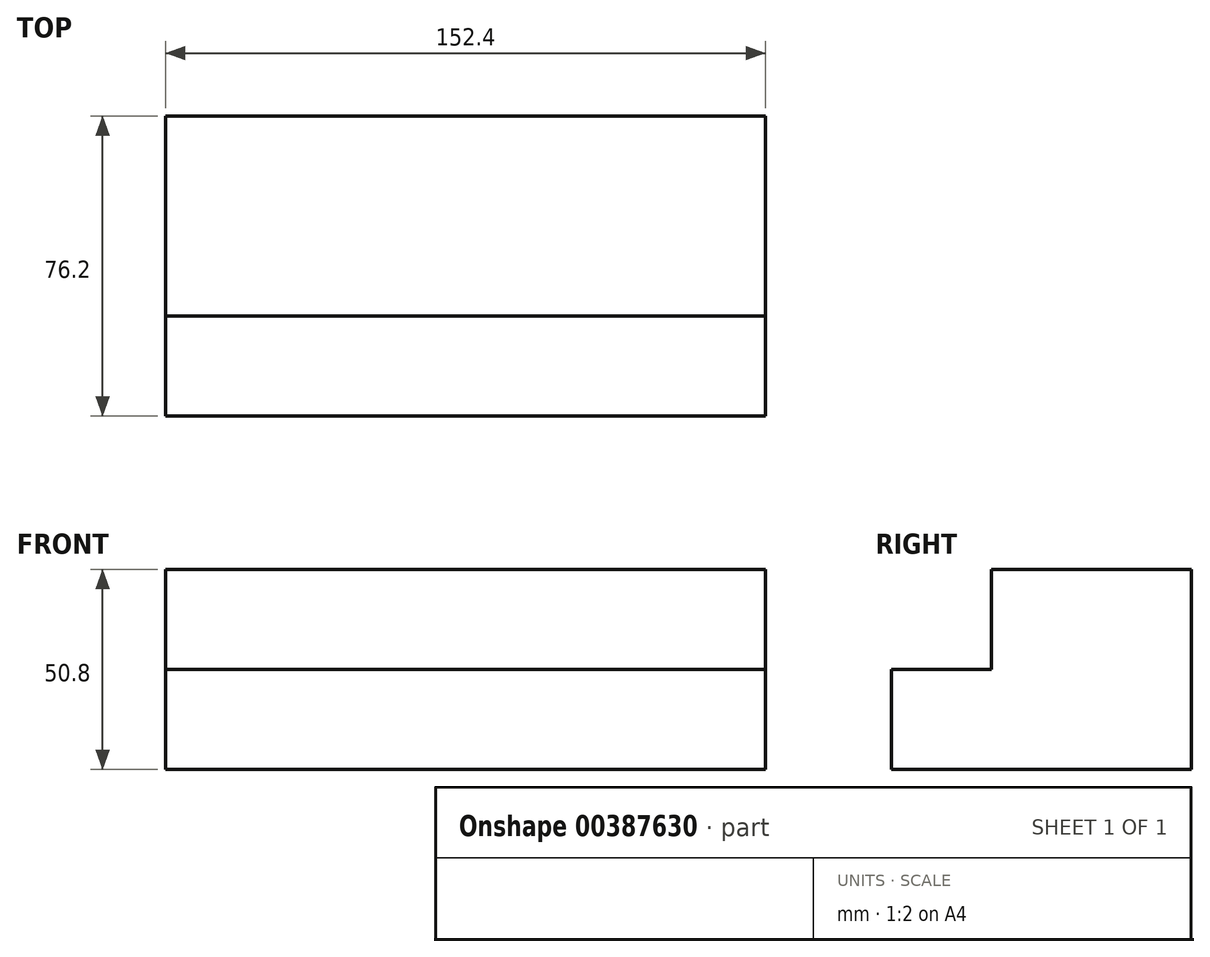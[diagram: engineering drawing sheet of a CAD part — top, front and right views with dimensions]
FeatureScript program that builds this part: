
annotation { "Feature Type Name" : "Feature", "Feature Type Description" : "" }
export const myFeature = defineFeature(function(context is Context, id is Id, definition is map)
    precondition{}
    {
        {
            var Q0;
            Q0=qCreatedBy(makeId("Top.planeOp"),FACE);
            var sketch = newSketch(context, id + "F0", { "sketchPlane" : qUnion([Q0])});
            skLineSegment(sketch, "E0.bottom", {"start": v(-152.4, -81.96) * mm, "end": v(0, -81.96) * mm});
            skLineSegment(sketch, "E0.top", {"start": v(-152.4, -5.76) * mm, "end": v(0, -5.76) * mm});
            skLineSegment(sketch, "E0.left", {"start": v(-152.4, -81.96) * mm, "end": v(-152.4, -5.76) * mm});
            skLineSegment(sketch, "E0.right", {"start": v(0, -81.96) * mm, "end": v(0, -5.76) * mm});
            skSolve(sketch);
        }
        {
            var Q0;
            Q0=qSketchRegion(id+"F0",true);
            extrude(context, id + "F1", {"entities" : qUnion([Q0]), "depth" : 25.4 * mm});
        }
        {
            var Q0;
            Q0=makeQuery(id+"F1.opExtrude","CAP_FACE",FACE,{"disambiguationData":[OSD([sQuery(id+"F0.wireOp",EDGE,"E0.bottom"),sQuery(id+"F0.wireOp",EDGE,"E0.top"),sQuery(id+"F0.wireOp",EDGE,"E0.left"),sQuery(id+"F0.wireOp",EDGE,"E0.right")])],"isStart":false});
            var sketch = newSketch(context, id + "F2", { "sketchPlane" : qUnion([Q0])});
            skLineSegment(sketch, "E1.bottom", {"start": v(-152.4, -5.76) * mm, "end": v(0, -5.76) * mm});
            skLineSegment(sketch, "E1.top", {"start": v(-152.4, -56.56) * mm, "end": v(0, -56.56) * mm});
            skLineSegment(sketch, "E1.left", {"start": v(-152.4, -5.76) * mm, "end": v(-152.4, -56.56) * mm});
            skLineSegment(sketch, "E1.right", {"start": v(0, -5.76) * mm, "end": v(0, -56.56) * mm});
            skSolve(sketch);
        }
        {
            var Q0;
            Q0=qSketchRegion(id+"F2",true);
            extrude(context, id + "F3", {"entities" : qUnion([Q0]), "operationType" : NewBodyOperationType.ADD, "depth" : 25.4 * mm});
        }
    });
